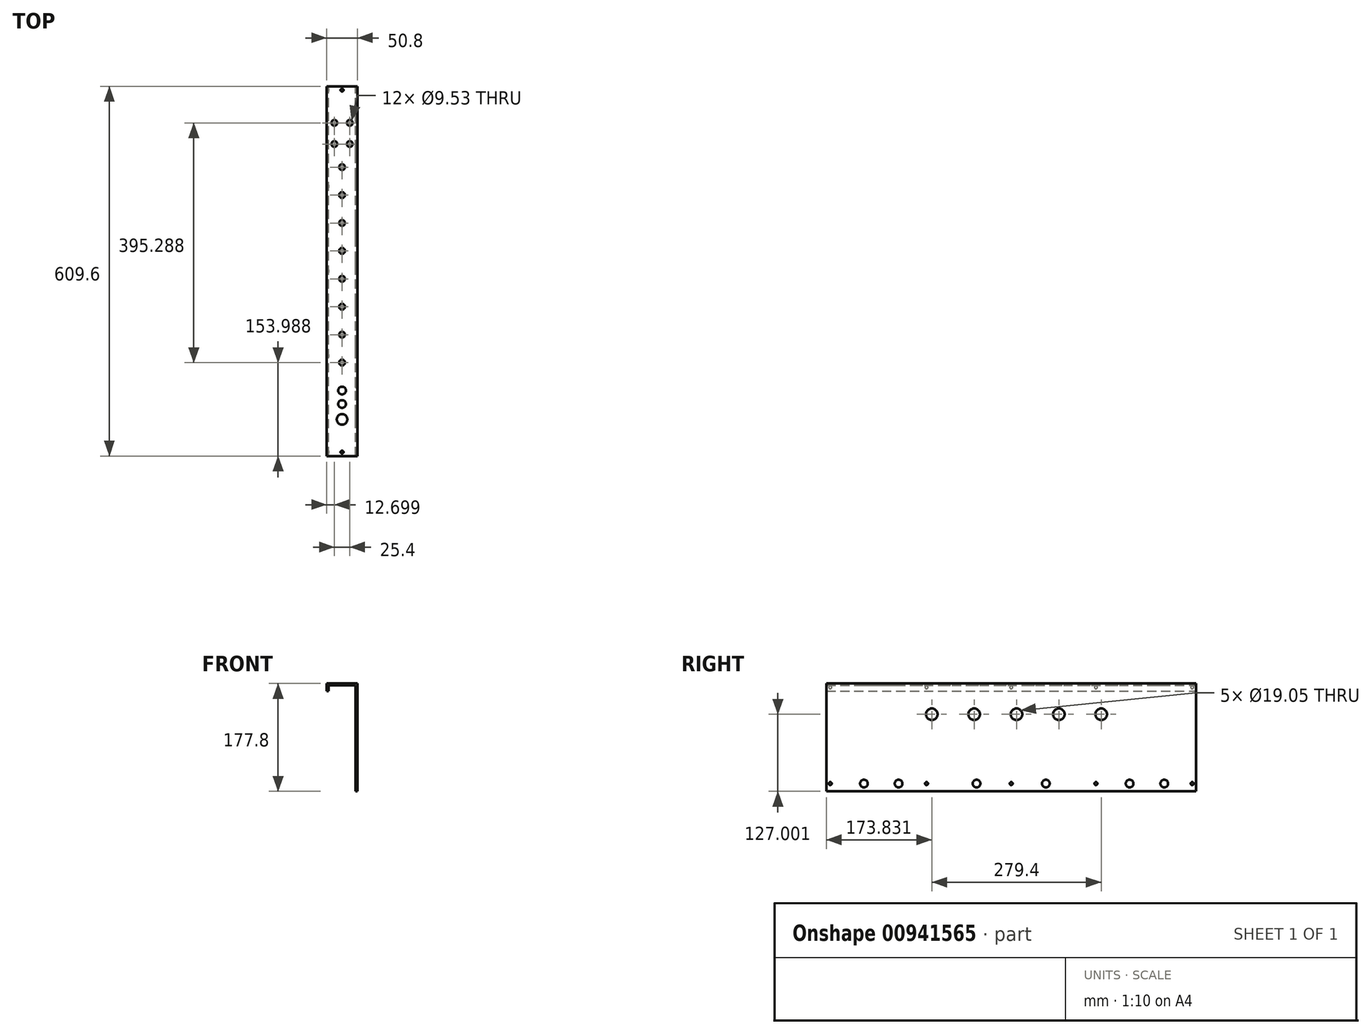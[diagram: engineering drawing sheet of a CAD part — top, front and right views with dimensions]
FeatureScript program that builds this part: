
annotation { "Feature Type Name" : "Feature", "Feature Type Description" : "" }
export const myFeature = defineFeature(function(context is Context, id is Id, definition is map)
    precondition{}
    {
        {
            var Q0;
            Q0=qCreatedBy(makeId("Front.planeOp"),FACE);
            var sketch = newSketch(context, id + "F0", { "sketchPlane" : qUnion([Q0])});
            skLineSegment(sketch, "E0", {"start": v(-27.92, 79.17) * mm, "end": v(-27.92, 91.87) * mm});
            skLineSegment(sketch, "E1", {"start": v(22.88, 91.87) * mm, "end": v(22.88, -85.93) * mm});
            skLineSegment(sketch, "E2", {"start": v(-27.92, 91.87) * mm, "end": v(22.88, 91.87) * mm});
            skLineSegment(sketch, "E3", {"start": v(-27.92, 79.17) * mm, "end": v(-24.75, 79.17) * mm});
            skLineSegment(sketch, "E4", {"start": v(-24.75, 79.17) * mm, "end": v(-24.75, 88.7) * mm});
            skLineSegment(sketch, "E5", {"start": v(-24.75, 88.7) * mm, "end": v(19.7, 88.7) * mm});
            skLineSegment(sketch, "E6", {"start": v(19.7, 88.7) * mm, "end": v(19.7, -85.93) * mm});
            skLineSegment(sketch, "E7", {"start": v(19.7, -85.93) * mm, "end": v(22.88, -85.93) * mm});
            skSolve(sketch);
        }
        {
            var Q0;
            Q0=makeQuery(id+"F0.imprint","IMPRINT",FACE,{"disambiguationData":[TD([[makeQuery(id+"F0.imprint","IMPRINT",EDGE,{"derivedFrom":sQuery(id+"F0.wireOp",EDGE,"E0")}),-1.0]])]});
            extrude(context, id + "F1", {"entities" : qUnion([Q0]), "depth" : 609.6 * mm, "offsetDistance" : 25.4 * mm});
        }
        {
            var Q0;
            Q0=makeQuery(id+"F1.opExtrude","SWEPT_FACE",FACE,{"disambiguationData":[OSD([sQuery(id+"F0.wireOp",EDGE,"E1")])]});
            var sketch = newSketch(context, id + "F2", { "sketchPlane" : qUnion([Q0])});
            skLineSegment(sketch, "E8", {"start": v(-609.6, 41.07) * mm, "end": v(0, 41.07) * mm, "construction": true});
            skPoint(sketch, "E9", {"position": v(-435.77, 41.07) * mm});
            skPoint(sketch, "E10", {"position": v(-365.92, 41.07) * mm});
            skPoint(sketch, "E11", {"position": v(-296.07, 41.07) * mm});
            skPoint(sketch, "E12", {"position": v(-226.22, 41.07) * mm});
            skPoint(sketch, "E13", {"position": v(-156.37, 41.07) * mm});
            skCircle(sketch, "E14", {"center": v(-156.37, 41.07) * mm, "radius": 9.53 * mm});
            skCircle(sketch, "E15", {"center": v(-226.22, 41.07) * mm, "radius": 9.53 * mm});
            skCircle(sketch, "E16", {"center": v(-296.07, 41.07) * mm, "radius": 9.53 * mm});
            skCircle(sketch, "E17", {"center": v(-365.92, 41.07) * mm, "radius": 9.53 * mm});
            skCircle(sketch, "E18", {"center": v(-435.77, 41.07) * mm, "radius": 9.53 * mm});
            skLineSegment(sketch, "E19", {"start": v(0, -73.23) * mm, "end": v(-609.6, -73.23) * mm, "construction": true});
            skCircle(sketch, "E20", {"center": v(-6.35, -73.23) * mm, "radius": 2.38 * mm});
            skCircle(sketch, "E21", {"center": v(-52.39, -73.23) * mm, "radius": 6.35 * mm});
            skCircle(sketch, "E22", {"center": v(-109.54, -73.23) * mm, "radius": 6.35 * mm});
            skCircle(sketch, "E23", {"center": v(-165.1, -73.23) * mm, "radius": 2.38 * mm});
            skCircle(sketch, "E24", {"center": v(-247.65, -73.23) * mm, "radius": 6.35 * mm});
            skCircle(sketch, "E25", {"center": v(-304.8, -73.23) * mm, "radius": 2.38 * mm});
            skCircle(sketch, "E26", {"center": v(-361.95, -73.23) * mm, "radius": 6.35 * mm});
            skCircle(sketch, "E27", {"center": v(-444.5, -73.23) * mm, "radius": 2.38 * mm});
            skCircle(sketch, "E28", {"center": v(-490.54, -73.23) * mm, "radius": 6.35 * mm});
            skCircle(sketch, "E29", {"center": v(-547.69, -73.23) * mm, "radius": 6.35 * mm});
            skCircle(sketch, "E30", {"center": v(-603.25, -73.23) * mm, "radius": 2.38 * mm});
            skLineSegment(sketch, "E31.0.0", {"start": v(0, 88.7) * mm, "end": v(0, -85.93) * mm});
            skLineSegment(sketch, "E31.0.1", {"start": v(0, -85.93) * mm, "end": v(-609.6, -85.93) * mm});
            skLineSegment(sketch, "E31.0.2", {"start": v(-609.6, -85.93) * mm, "end": v(-609.6, 88.7) * mm});
            skLineSegment(sketch, "E31.0.3", {"start": v(-609.6, 88.7) * mm, "end": v(0, 88.7) * mm});
            skSolve(sketch);
        }
        {
            var Q0;
            Q0=makeQuery(id+"F2.imprint","IMPRINT",FACE,{"disambiguationData":[TD([[makeQuery(id+"F2.imprint","IMPRINT",EDGE,{"derivedFrom":sQuery(id+"F2.wireOp",EDGE,"E18")}),1.0]])]});
            var Q1;
            Q1=makeQuery(id+"F2.imprint","IMPRINT",FACE,{"disambiguationData":[TD([[makeQuery(id+"F2.imprint","IMPRINT",EDGE,{"derivedFrom":sQuery(id+"F2.wireOp",EDGE,"E17")}),1.0]])]});
            var Q2;
            Q2=makeQuery(id+"F2.imprint","IMPRINT",FACE,{"disambiguationData":[TD([[makeQuery(id+"F2.imprint","IMPRINT",EDGE,{"derivedFrom":sQuery(id+"F2.wireOp",EDGE,"E16")}),1.0]])]});
            var Q3;
            Q3=makeQuery(id+"F2.imprint","IMPRINT",FACE,{"disambiguationData":[TD([[makeQuery(id+"F2.imprint","IMPRINT",EDGE,{"derivedFrom":sQuery(id+"F2.wireOp",EDGE,"E15")}),1.0]])]});
            var Q4;
            Q4=makeQuery(id+"F2.imprint","IMPRINT",FACE,{"disambiguationData":[TD([[makeQuery(id+"F2.imprint","IMPRINT",EDGE,{"derivedFrom":sQuery(id+"F2.wireOp",EDGE,"E14")}),1.0]])]});
            var Q5;
            Q5=makeQuery(id+"F2.imprint","IMPRINT",FACE,{"disambiguationData":[TD([[makeQuery(id+"F2.imprint","IMPRINT",EDGE,{"derivedFrom":sQuery(id+"F2.wireOp",EDGE,"E30")}),1.0]])]});
            var Q6;
            Q6=makeQuery(id+"F2.imprint","IMPRINT",FACE,{"disambiguationData":[TD([[makeQuery(id+"F2.imprint","IMPRINT",EDGE,{"derivedFrom":sQuery(id+"F2.wireOp",EDGE,"E29")}),1.0]])]});
            var Q7;
            Q7=makeQuery(id+"F2.imprint","IMPRINT",FACE,{"disambiguationData":[TD([[makeQuery(id+"F2.imprint","IMPRINT",EDGE,{"derivedFrom":sQuery(id+"F2.wireOp",EDGE,"E28")}),1.0]])]});
            var Q8;
            Q8=makeQuery(id+"F2.imprint","IMPRINT",FACE,{"disambiguationData":[TD([[makeQuery(id+"F2.imprint","IMPRINT",EDGE,{"derivedFrom":sQuery(id+"F2.wireOp",EDGE,"E26")}),1.0]])]});
            var Q9;
            Q9=makeQuery(id+"F2.imprint","IMPRINT",FACE,{"disambiguationData":[TD([[makeQuery(id+"F2.imprint","IMPRINT",EDGE,{"derivedFrom":sQuery(id+"F2.wireOp",EDGE,"E27")}),1.0]])]});
            var Q10;
            Q10=makeQuery(id+"F2.imprint","IMPRINT",FACE,{"disambiguationData":[TD([[makeQuery(id+"F2.imprint","IMPRINT",EDGE,{"derivedFrom":sQuery(id+"F2.wireOp",EDGE,"E25")}),1.0]])]});
            var Q11;
            Q11=makeQuery(id+"F2.imprint","IMPRINT",FACE,{"disambiguationData":[TD([[makeQuery(id+"F2.imprint","IMPRINT",EDGE,{"derivedFrom":sQuery(id+"F2.wireOp",EDGE,"E24")}),1.0]])]});
            var Q12;
            Q12=makeQuery(id+"F2.imprint","IMPRINT",FACE,{"disambiguationData":[TD([[makeQuery(id+"F2.imprint","IMPRINT",EDGE,{"derivedFrom":sQuery(id+"F2.wireOp",EDGE,"E23")}),1.0]])]});
            var Q13;
            Q13=makeQuery(id+"F2.imprint","IMPRINT",FACE,{"disambiguationData":[TD([[makeQuery(id+"F2.imprint","IMPRINT",EDGE,{"derivedFrom":sQuery(id+"F2.wireOp",EDGE,"E22")}),1.0]])]});
            var Q14;
            Q14=makeQuery(id+"F2.imprint","IMPRINT",FACE,{"disambiguationData":[TD([[makeQuery(id+"F2.imprint","IMPRINT",EDGE,{"derivedFrom":sQuery(id+"F2.wireOp",EDGE,"E21")}),1.0]])]});
            var Q15;
            Q15=makeQuery(id+"F2.imprint","IMPRINT",FACE,{"disambiguationData":[TD([[makeQuery(id+"F2.imprint","IMPRINT",EDGE,{"derivedFrom":sQuery(id+"F2.wireOp",EDGE,"E20")}),1.0]])]});
            var Q16;
            Q16=sQuery(id+"F2.wireOp",EDGE,"E18");
            var Q17;
            Q17=sQuery(id+"F2.wireOp",EDGE,"E17");
            var Q18;
            Q18=sQuery(id+"F2.wireOp",EDGE,"E16");
            var Q19;
            Q19=sQuery(id+"F2.wireOp",EDGE,"E15");
            var Q20;
            Q20=sQuery(id+"F2.wireOp",EDGE,"E14");
            var Q21;
            Q21=sQuery(id+"F2.wireOp",EDGE,"E30");
            var Q22;
            Q22=sQuery(id+"F2.wireOp",EDGE,"E29");
            var Q23;
            Q23=sQuery(id+"F2.wireOp",EDGE,"E28");
            var Q24;
            Q24=sQuery(id+"F2.wireOp",EDGE,"E27");
            var Q25;
            Q25=sQuery(id+"F2.wireOp",EDGE,"E26");
            var Q26;
            Q26=sQuery(id+"F2.wireOp",EDGE,"E25");
            var Q27;
            Q27=sQuery(id+"F2.wireOp",EDGE,"E24");
            var Q28;
            Q28=sQuery(id+"F2.wireOp",EDGE,"E23");
            var Q29;
            Q29=sQuery(id+"F2.wireOp",EDGE,"E22");
            var Q30;
            Q30=sQuery(id+"F2.wireOp",EDGE,"E21");
            var Q31;
            Q31=sQuery(id+"F2.wireOp",EDGE,"E20");
            extrude(context, id + "F3", {"entities" : qUnion([Q0, Q1, Q2, Q3, Q4, Q5, Q6, Q7, Q8, Q9, Q10, Q11, Q12, Q13, Q14, Q15]), "operationType" : NewBodyOperationType.REMOVE, "surfaceEntities" : qUnion([Q16, Q17, Q18, Q19, Q20, Q21, Q22, Q23, Q24, Q25, Q26, Q27, Q28, Q29, Q30, Q31]), "endBound" : BoundingType.THROUGH_ALL, "oppositeDirection" : true, "depth" : 25.4 * mm, "offsetDistance" : 25.4 * mm});
        }
        {
            var Q0;
            Q0=makeQuery(id+"F1.opExtrude","SWEPT_FACE",FACE,{"disambiguationData":[OSD([sQuery(id+"F0.wireOp",EDGE,"E0")])]});
            var sketch = newSketch(context, id + "F4", { "sketchPlane" : qUnion([Q0])});
            skLineSegment(sketch, "E32", {"start": v(0, 85.52) * mm, "end": v(609.6, 85.52) * mm, "construction": true});
            skCircle(sketch, "E33", {"center": v(6.35, 85.52) * mm, "radius": 2.38 * mm});
            skCircle(sketch, "E34", {"center": v(165.1, 85.52) * mm, "radius": 2.38 * mm});
            skCircle(sketch, "E35", {"center": v(304.8, 85.52) * mm, "radius": 2.38 * mm});
            skCircle(sketch, "E36", {"center": v(444.5, 85.52) * mm, "radius": 2.38 * mm});
            skCircle(sketch, "E37", {"center": v(603.25, 85.52) * mm, "radius": 2.38 * mm});
            skSolve(sketch);
        }
        {
            var Q0;
            Q0 = qSketchRegion(id + "F4", true);
            extrude(context, id + "F5", {"entities" : qUnion([Q0]), "operationType" : NewBodyOperationType.REMOVE, "endBound" : BoundingType.UP_TO_NEXT, "oppositeDirection" : true, "depth" : 25.4 * mm, "offsetDistance" : 25.4 * mm});
        }
        {
            var Q0;
            Q0=makeQuery(id+"F1.opExtrude","SWEPT_FACE",FACE,{"disambiguationData":[OSD([sQuery(id+"F0.wireOp",EDGE,"E2")])]});
            var sketch = newSketch(context, id + "F6", { "sketchPlane" : qUnion([Q0])});
            skLineSegment(sketch, "E38", {"start": v(-2.52, 0) * mm, "end": v(-2.52, -609.6) * mm, "construction": true});
            skCircle(sketch, "E39", {"center": v(10.18, -60.33) * mm, "radius": 4.76 * mm});
            skCircle(sketch, "E40", {"center": v(-15.22, -60.33) * mm, "radius": 4.76 * mm});
            skCircle(sketch, "E41", {"center": v(10.18, -95.25) * mm, "radius": 4.76 * mm});
            skCircle(sketch, "E42", {"center": v(-15.22, -95.25) * mm, "radius": 4.76 * mm});
            skCircle(sketch, "E43", {"center": v(-2.52, -133.35) * mm, "radius": 4.76 * mm});
            skCircle(sketch, "E44", {"center": v(-2.52, -179.39) * mm, "radius": 4.76 * mm});
            skCircle(sketch, "E45", {"center": v(-2.52, -225.43) * mm, "radius": 4.76 * mm});
            skCircle(sketch, "E46", {"center": v(-2.52, -317.5) * mm, "radius": 4.76 * mm});
            skCircle(sketch, "E47", {"center": v(-2.52, -409.58) * mm, "radius": 4.76 * mm});
            skCircle(sketch, "E48", {"center": v(-2.52, -501.65) * mm, "radius": 6.35 * mm});
            skCircle(sketch, "E49", {"center": v(-2.52, -363.54) * mm, "radius": 4.76 * mm});
            skCircle(sketch, "E50", {"center": v(-2.52, -271.46) * mm, "radius": 4.76 * mm});
            skCircle(sketch, "E51", {"center": v(-2.52, -523.88) * mm, "radius": 6.35 * mm});
            skCircle(sketch, "E52", {"center": v(-2.52, -549.28) * mm, "radius": 8.73 * mm});
            skCircle(sketch, "E53", {"center": v(-2.52, -455.61) * mm, "radius": 4.76 * mm});
            skCircle(sketch, "E54", {"center": v(-2.52, -6.35) * mm, "radius": 2.38 * mm});
            skCircle(sketch, "E55", {"center": v(-2.52, -603.25) * mm, "radius": 2.38 * mm});
            skSolve(sketch);
        }
        {
            var Q0;
            Q0 = qSketchRegion(id + "F6", true);
            extrude(context, id + "F7", {"entities" : qUnion([Q0]), "operationType" : NewBodyOperationType.REMOVE, "endBound" : BoundingType.UP_TO_NEXT, "oppositeDirection" : true, "depth" : 25.4 * mm, "offsetDistance" : 25.4 * mm});
        }
    });
